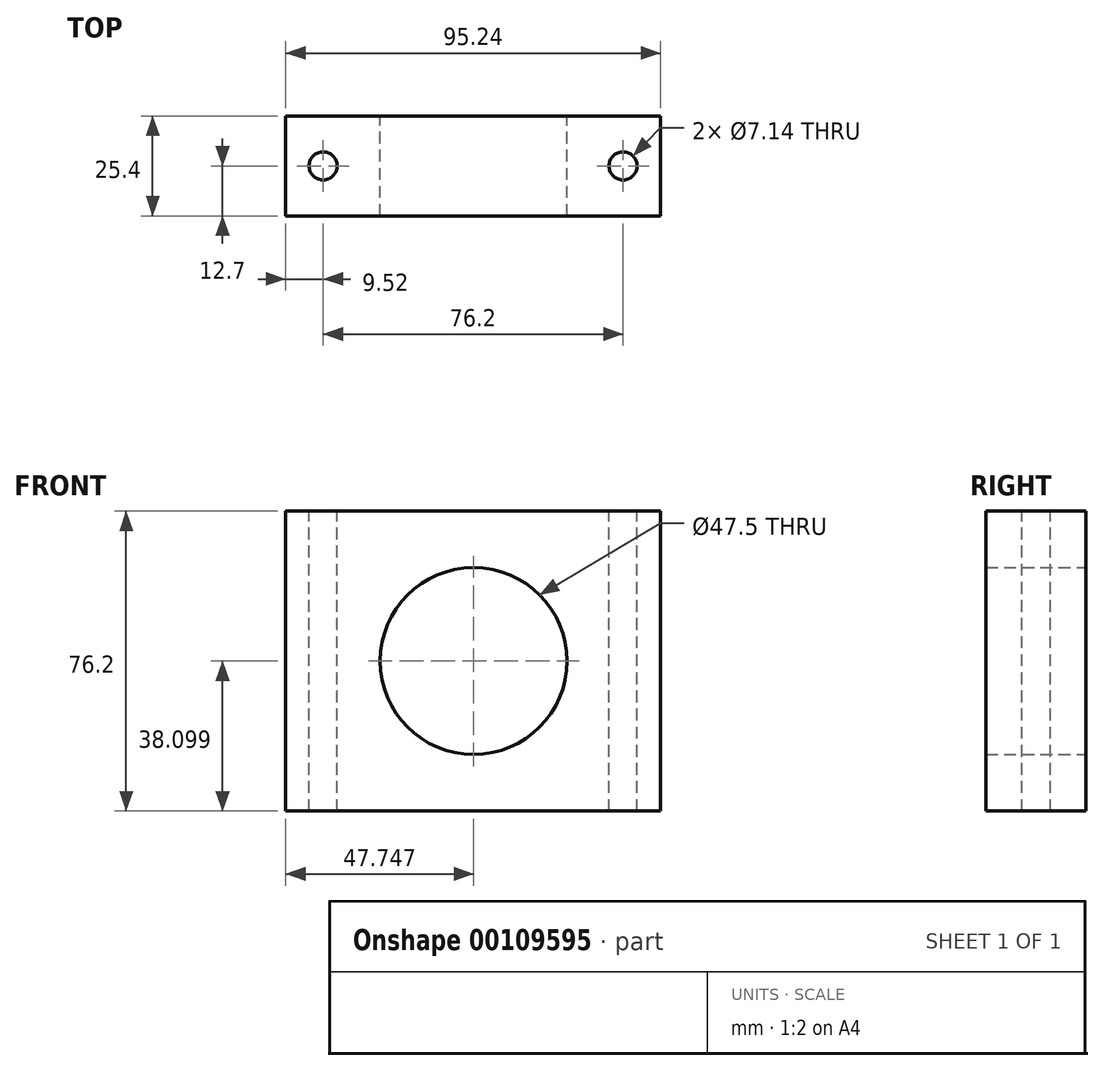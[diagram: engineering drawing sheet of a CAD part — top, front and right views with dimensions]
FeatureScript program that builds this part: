
annotation { "Feature Type Name" : "Feature", "Feature Type Description" : "" }
export const myFeature = defineFeature(function(context is Context, id is Id, definition is map)
    precondition{}
    {
        {
            var Q0;
            Q0=qCreatedBy(makeId("Front.planeOp"),FACE);
            var sketch = newSketch(context, id + "F0", { "sketchPlane" : qUnion([Q0])});
            skLineSegment(sketch, "E0.bottom", {"start": v(47.63, -58.1) * mm, "end": v(-47.62, -58.1) * mm});
            skLineSegment(sketch, "E0.top", {"start": v(47.63, 18.1) * mm, "end": v(-47.63, 18.1) * mm});
            skLineSegment(sketch, "E0.left", {"start": v(47.63, -58.1) * mm, "end": v(47.62, 18.1) * mm});
            skLineSegment(sketch, "E0.right", {"start": v(-47.62, -58.1) * mm, "end": v(-47.63, 18.1) * mm});
            skPoint(sketch, "E0.middle", {"position": v(0, -20) * mm});
            skSolve(sketch);
        }
        {
            var Q0;
            Q0 = qSketchRegion(id + "F0", true);
            extrude(context, id + "F1", {"entities" : qUnion([Q0]), "depth" : 25.4 * mm});
        }
        {
            var Q0;
            Q0=makeQuery(id+"F1.opExtrude","CAP_FACE",FACE,{"disambiguationData":[OSD([sQuery(id+"F0.wireOp",EDGE,"E0.bottom"),sQuery(id+"F0.wireOp",EDGE,"E0.top"),sQuery(id+"F0.wireOp",EDGE,"E0.left"),sQuery(id+"F0.wireOp",EDGE,"E0.right")])],"isStart":true});
            var sketch = newSketch(context, id + "F2", { "sketchPlane" : qUnion([Q0])});
            skCircle(sketch, "E1", {"center": v(-0.13, -20) * mm, "radius": 23.75 * mm});
            skSolve(sketch);
        }
        {
            var Q0;
            Q0 = qSketchRegion(id + "F2", true);
            var Q1;
            Q1=makeQuery(id+"F1.opExtrude","CAP_FACE",FACE,{"disambiguationData":[OSD([sQuery(id+"F0.wireOp",EDGE,"E0.bottom"),sQuery(id+"F0.wireOp",EDGE,"E0.top"),sQuery(id+"F0.wireOp",EDGE,"E0.left"),sQuery(id+"F0.wireOp",EDGE,"E0.right")])],"isStart":false});
            extrude(context, id + "F3", {"entities" : qUnion([Q0]), "operationType" : NewBodyOperationType.REMOVE, "endBound" : BoundingType.UP_TO_SURFACE, "oppositeDirection" : true, "endBoundEntityFace" : qUnion([Q1]), "depth" : 25.4 * mm});
        }
        {
            var Q0;
            Q0=makeQuery(id+"F1.opExtrude","SWEPT_FACE",FACE,{"disambiguationData":[OSD([sQuery(id+"F0.wireOp",EDGE,"E0.top")])]});
            var sketch = newSketch(context, id + "F4", { "sketchPlane" : qUnion([Q0])});
            skCircle(sketch, "E2", {"center": v(-38.1, -12.7) * mm, "radius": 3.57 * mm});
            skCircle(sketch, "E3", {"center": v(38.1, -12.7) * mm, "radius": 3.57 * mm});
            skPoint(sketch, "E3.centerSnap0", {"position": v(47.62, -12.7) * mm});
            skSolve(sketch);
        }
        {
            var Q0;
            Q0 = qSketchRegion(id + "F4", true);
            var Q1;
            Q1=makeQuery(id+"F1.opExtrude","SWEPT_FACE",FACE,{"disambiguationData":[OSD([sQuery(id+"F0.wireOp",EDGE,"E0.bottom")])]});
            extrude(context, id + "F5", {"entities" : qUnion([Q0]), "operationType" : NewBodyOperationType.REMOVE, "endBound" : BoundingType.UP_TO_SURFACE, "oppositeDirection" : true, "endBoundEntityFace" : qUnion([Q1]), "depth" : 25.4 * mm});
        }
    });
